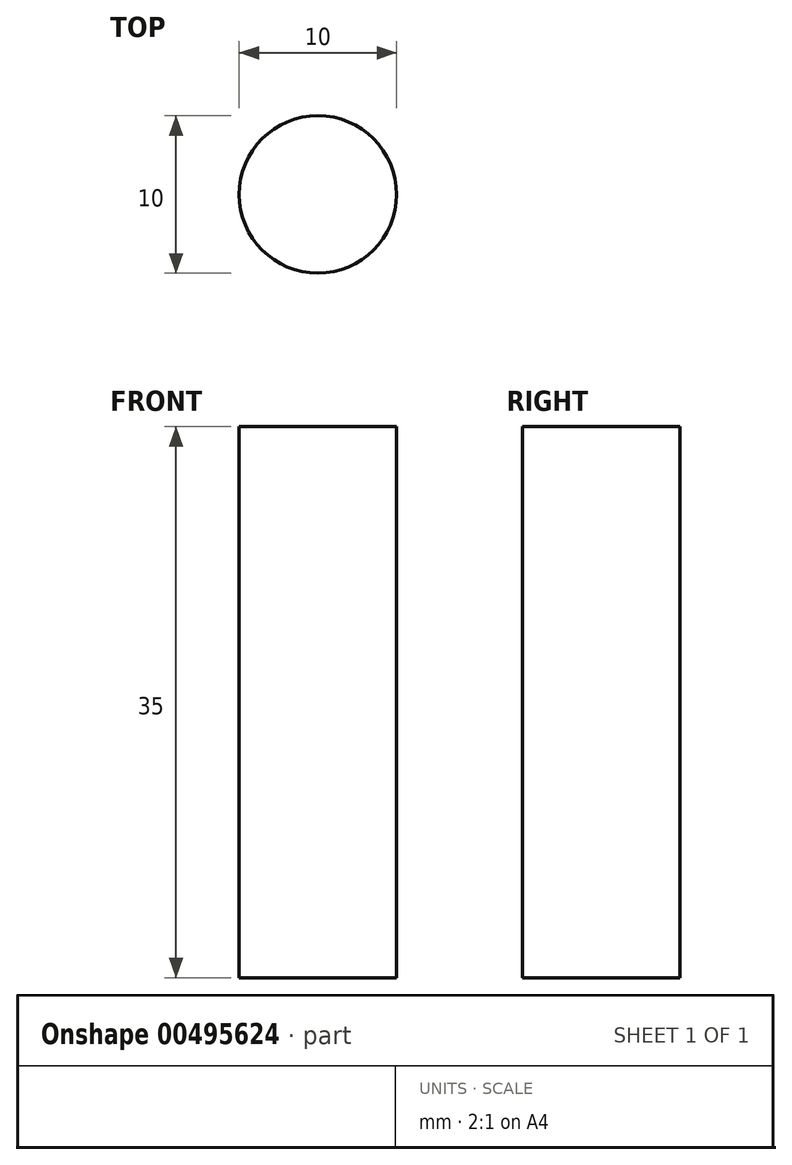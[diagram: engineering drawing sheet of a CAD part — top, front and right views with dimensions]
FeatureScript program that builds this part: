
annotation { "Feature Type Name" : "Feature", "Feature Type Description" : "" }
export const myFeature = defineFeature(function(context is Context, id is Id, definition is map)
    precondition{}
    {
        {
            var Q0;
            Q0=qCreatedBy(makeId("Top.planeOp"),FACE);
            var sketch = newSketch(context, id + "F0", { "sketchPlane" : qUnion([Q0])});
            skCircle(sketch, "E0", {"center": v(-13.76, -3.8) * mm, "radius": 5 * mm});
            skSolve(sketch);
        }
        {
            var Q0;
            Q0 = qSketchRegion(id + "F0", true);
            extrude(context, id + "F1", {"entities" : qUnion([Q0]), "depth" : 35 * mm});
        }
    });
